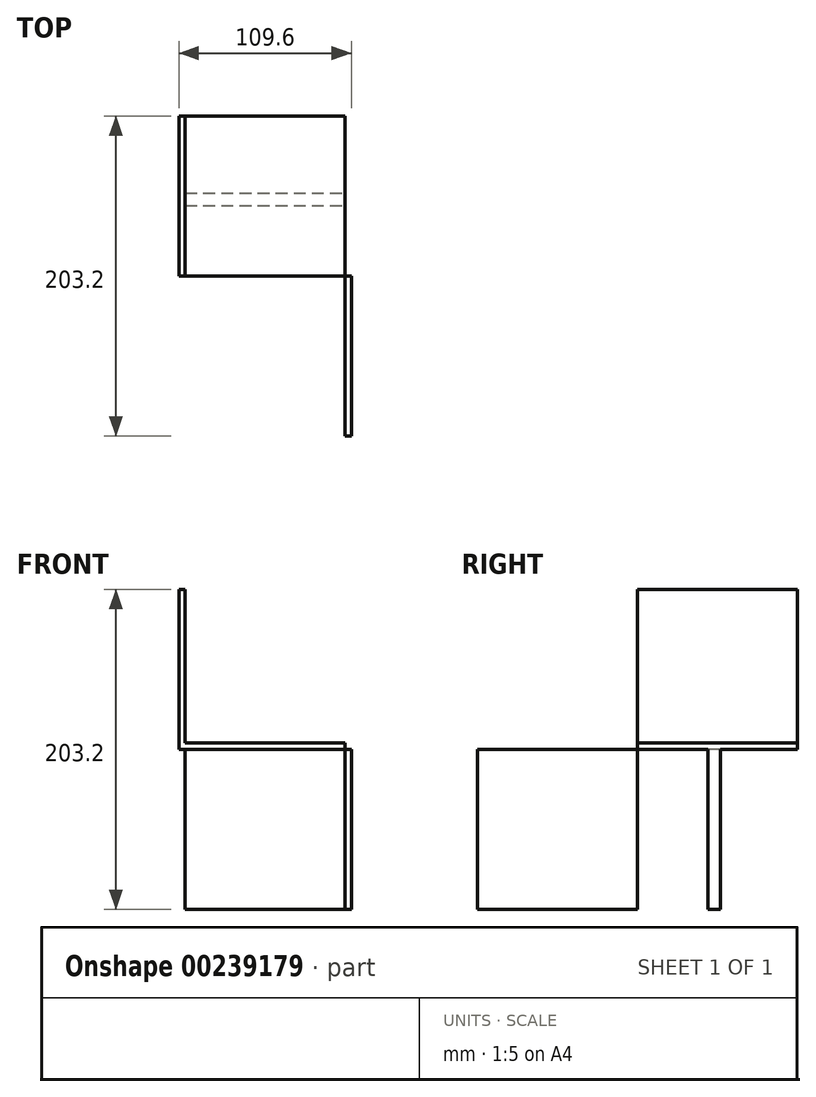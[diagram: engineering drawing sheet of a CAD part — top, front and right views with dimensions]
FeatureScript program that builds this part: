
annotation { "Feature Type Name" : "Feature", "Feature Type Description" : "" }
export const myFeature = defineFeature(function(context is Context, id is Id, definition is map)
    precondition{}
    {
        {
            assignVariable(context, id + "F0", {"name" : "W", "anyValue" : 4});
        }
        {
            var Q0;
            Q0=qCreatedBy(makeId("Front.planeOp"),FACE);
            var sketch = newSketch(context, id + "F1", { "sketchPlane" : qUnion([Q0])});
            skLineSegment(sketch, "E0.bottom", {"start": v(-50.8, 50.8) * mm, "end": v(50.8, 50.8) * mm});
            skLineSegment(sketch, "E0.top", {"start": v(-50.8, -50.8) * mm, "end": v(50.8, -50.8) * mm});
            skLineSegment(sketch, "E0.left", {"start": v(-50.8, 50.8) * mm, "end": v(-50.8, -50.8) * mm});
            skLineSegment(sketch, "E0.right", {"start": v(50.8, 50.8) * mm, "end": v(50.8, -50.8) * mm});
            skPoint(sketch, "E0.middle", {"position": v(0, 0) * mm});
            skSolve(sketch);
        }
        {
            var Q0;
            Q0 = qSketchRegion(id + "F1", true);
            extrude(context, id + "F2", {"entities" : qUnion([Q0]), "endBound" : BoundingType.SYMMETRIC, "depth" : (getVariable(context, 'W')) * mm});
        }
        {
            var Q0;
            Q0=makeQuery(id+"F2.opExtrude","CAP_FACE",FACE,{"disambiguationData":[OSD([sQuery(id+"F1.wireOp",EDGE,"E0.bottom"),sQuery(id+"F1.wireOp",EDGE,"E0.top"),sQuery(id+"F1.wireOp",EDGE,"E0.left"),sQuery(id+"F1.wireOp",EDGE,"E0.right")])],"isStart":false});
            var sketch = newSketch(context, id + "F3", { "sketchPlane" : qUnion([Q0])});
            skLineSegment(sketch, "E1.bottom", {"start": v(-50.8, 50.8) * mm, "end": v(50.8, 50.8) * mm});
            skLineSegment(sketch, "E1.top", {"start": v(-50.8, -50.8) * mm, "end": v(50.8, -50.8) * mm});
            skLineSegment(sketch, "E1.left", {"start": v(-50.8, 50.8) * mm, "end": v(-50.8, -50.8) * mm});
            skLineSegment(sketch, "E1.right", {"start": v(50.8, 50.8) * mm, "end": v(50.8, -50.8) * mm});
            skPoint(sketch, "E1.middle", {"position": v(0, 0) * mm});
            skSolve(sketch);
        }
        {
            var Q0;
            Q0 = qSketchRegion(id + "F3", true);
            extrude(context, id + "F4", {"entities" : qUnion([Q0]), "operationType" : NewBodyOperationType.ADD, "depth" : (getVariable(context, 'W')) * mm});
        }
        {
            var Q0;
            Q0=makeQuery(id+"F4.boolean.opBoolean","MERGE",FACE,{"derivedFrom":[makeQuery(id+"F2.opExtrude","SWEPT_FACE",FACE,{"disambiguationData":[OSD([sQuery(id+"F1.wireOp",EDGE,"E0.right")])]}),makeQuery(id+"F4.opExtrude","SWEPT_FACE",FACE,{"disambiguationData":[OSD([sQuery(id+"F3.wireOp",EDGE,"E1.right")])]})]});
            var sketch = newSketch(context, id + "F5", { "sketchPlane" : qUnion([Q0])});
            skLineSegment(sketch, "E2.bottom", {"start": v(-50.8, 50.8) * mm, "end": v(-152.4, 50.8) * mm});
            skLineSegment(sketch, "E2.top", {"start": v(-50.8, -50.8) * mm, "end": v(-152.4, -50.8) * mm});
            skLineSegment(sketch, "E2.left", {"start": v(-50.8, 50.8) * mm, "end": v(-50.8, -50.8) * mm});
            skLineSegment(sketch, "E2.right", {"start": v(-152.4, 50.8) * mm, "end": v(-152.4, -50.8) * mm});
            skSolve(sketch);
        }
        {
            var Q0;
            Q0 = qSketchRegion(id + "F5", true);
            extrude(context, id + "F6", {"entities" : qUnion([Q0]), "operationType" : NewBodyOperationType.ADD, "depth" : (getVariable(context, 'W')) * mm});
        }
        {
            var Q0;
            Q0=makeQuery(id+"F6.boolean.opBoolean","MERGE",FACE,{"derivedFrom":[makeQuery(id+"F4.boolean.opBoolean","MERGE",FACE,{"derivedFrom":[makeQuery(id+"F2.opExtrude","SWEPT_FACE",FACE,{"disambiguationData":[OSD([sQuery(id+"F1.wireOp",EDGE,"E0.bottom")])]}),makeQuery(id+"F4.opExtrude","SWEPT_FACE",FACE,{"disambiguationData":[OSD([sQuery(id+"F3.wireOp",EDGE,"E1.bottom")])]})]}),makeQuery(id+"F6.opExtrude","SWEPT_FACE",FACE,{"disambiguationData":[OSD([sQuery(id+"F5.wireOp",EDGE,"E2.bottom")])]})]});
            var sketch = newSketch(context, id + "F7", { "sketchPlane" : qUnion([Q0])});
            skLineSegment(sketch, "E3.bottom", {"start": v(-50.8, 50.8) * mm, "end": v(50.8, 50.8) * mm});
            skLineSegment(sketch, "E3.top", {"start": v(-50.8, -50.8) * mm, "end": v(50.8, -50.8) * mm});
            skLineSegment(sketch, "E3.left", {"start": v(-50.8, 50.8) * mm, "end": v(-50.8, -50.8) * mm});
            skLineSegment(sketch, "E3.right", {"start": v(50.8, 50.8) * mm, "end": v(50.8, -50.8) * mm});
            skSolve(sketch);
        }
        {
            var Q0;
            Q0 = qSketchRegion(id + "F7", true);
            extrude(context, id + "F8", {"entities" : qUnion([Q0]), "operationType" : NewBodyOperationType.ADD, "depth" : (getVariable(context, 'W')) * mm});
        }
        {
            var Q0;
            Q0=makeQuery(id+"F8.boolean.opBoolean","MERGE",FACE,{"derivedFrom":[makeQuery(id+"F4.boolean.opBoolean","MERGE",FACE,{"derivedFrom":[makeQuery(id+"F2.opExtrude","SWEPT_FACE",FACE,{"disambiguationData":[OSD([sQuery(id+"F1.wireOp",EDGE,"E0.left")])]}),makeQuery(id+"F4.opExtrude","SWEPT_FACE",FACE,{"disambiguationData":[OSD([sQuery(id+"F3.wireOp",EDGE,"E1.left")])]})]}),makeQuery(id+"F8.opExtrude","SWEPT_FACE",FACE,{"disambiguationData":[OSD([sQuery(id+"F7.wireOp",EDGE,"E3.left")])]})]});
            var sketch = newSketch(context, id + "F9", { "sketchPlane" : qUnion([Q0])});
            skLineSegment(sketch, "E4.bottom", {"start": v(-50.8, 152.4) * mm, "end": v(50.8, 152.4) * mm});
            skLineSegment(sketch, "E4.top", {"start": v(-50.8, 50.8) * mm, "end": v(50.8, 50.8) * mm});
            skLineSegment(sketch, "E4.left", {"start": v(-50.8, 152.4) * mm, "end": v(-50.8, 50.8) * mm});
            skLineSegment(sketch, "E4.right", {"start": v(50.8, 152.4) * mm, "end": v(50.8, 50.8) * mm});
            skSolve(sketch);
        }
        {
            var Q0;
            Q0 = qSketchRegion(id + "F9", true);
            extrude(context, id + "F10", {"entities" : qUnion([Q0]), "operationType" : NewBodyOperationType.ADD, "depth" : (getVariable(context, 'W')) * mm});
        }
    });
